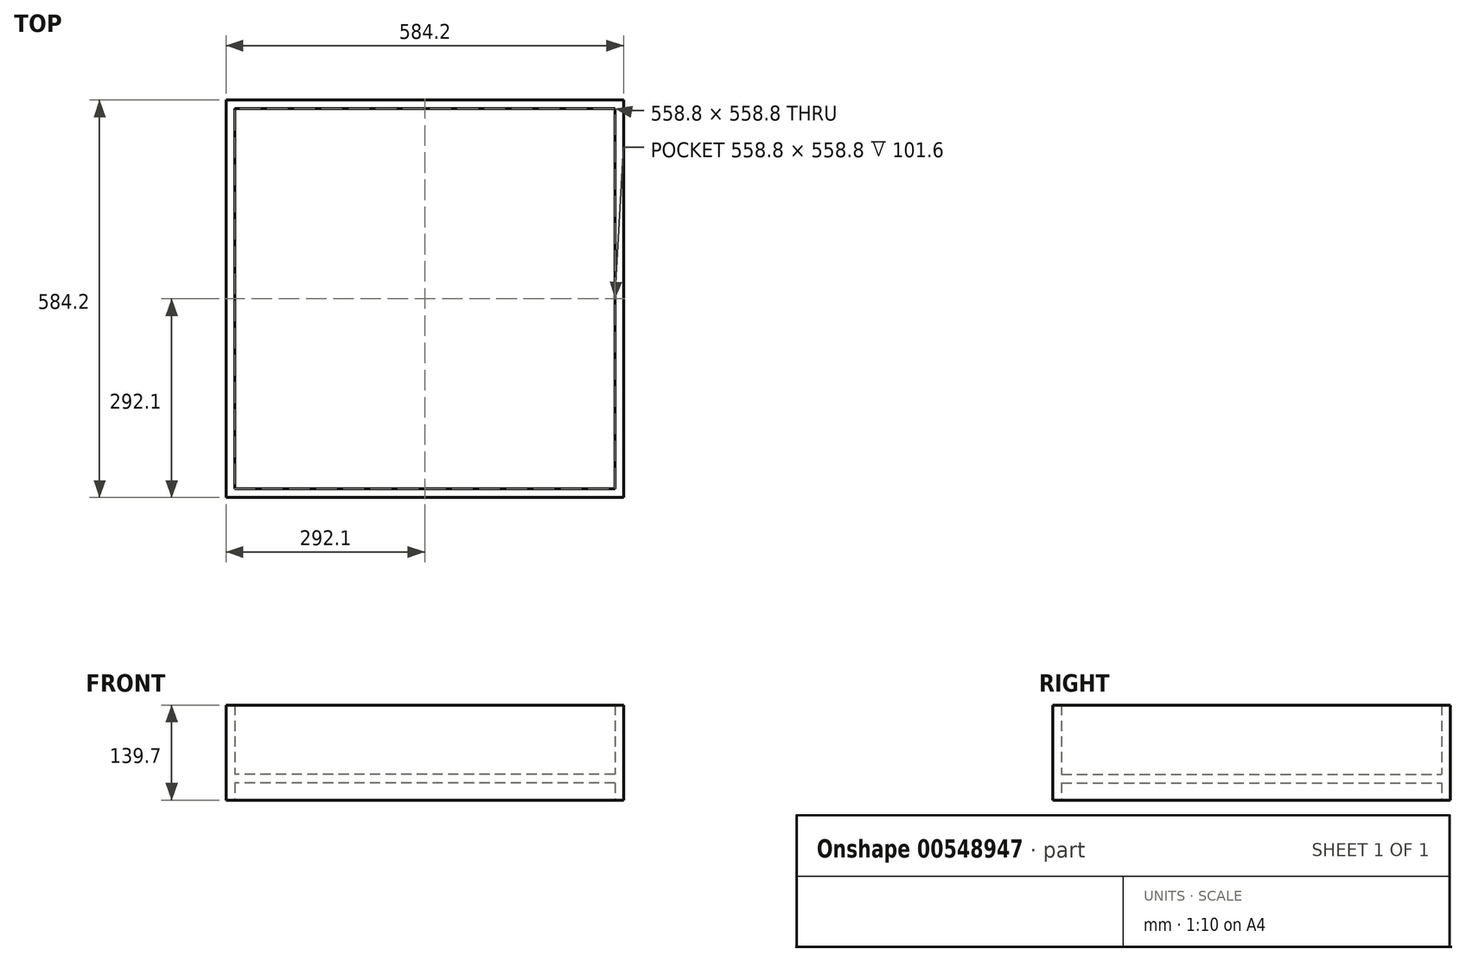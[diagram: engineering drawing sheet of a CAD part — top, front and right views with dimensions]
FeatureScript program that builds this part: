
annotation { "Feature Type Name" : "Feature", "Feature Type Description" : "" }
export const myFeature = defineFeature(function(context is Context, id is Id, definition is map)
    precondition{}
    {
        {
            var Q0;
            Q0=qCreatedBy(makeId("Top.planeOp"),FACE);
            var sketch = newSketch(context, id + "F0", { "sketchPlane" : qUnion([Q0])});
            skLineSegment(sketch, "E0.bottom", {"start": v(-292.1, 292.1) * mm, "end": v(292.1, 292.1) * mm});
            skLineSegment(sketch, "E0.top", {"start": v(-292.1, -292.1) * mm, "end": v(292.1, -292.1) * mm});
            skLineSegment(sketch, "E0.left", {"start": v(-292.1, 292.1) * mm, "end": v(-292.1, -292.1) * mm});
            skLineSegment(sketch, "E0.right", {"start": v(292.1, 292.1) * mm, "end": v(292.1, -292.1) * mm});
            skPoint(sketch, "E0.middle", {"position": v(0, 0) * mm});
            skSolve(sketch);
        }
        {
            var Q0;
            Q0 = qSketchRegion(id + "F0", true);
            extrude(context, id + "F1", {"entities" : qUnion([Q0]), "depth" : 12.7 * mm, "offsetDistance" : 25.4 * mm});
        }
        {
            var Q0;
            Q0=makeQuery(id+"F1.opExtrude","CAP_FACE",FACE,{"disambiguationData":[OSD([sQuery(id+"F0.wireOp",EDGE,"E0.bottom"),sQuery(id+"F0.wireOp",EDGE,"E0.top"),sQuery(id+"F0.wireOp",EDGE,"E0.left"),sQuery(id+"F0.wireOp",EDGE,"E0.right")])],"isStart":false});
            var sketch = newSketch(context, id + "F2", { "sketchPlane" : qUnion([Q0])});
            skLineSegment(sketch, "E1.bottom", {"start": v(-292.1, 292.1) * mm, "end": v(292.1, 292.1) * mm});
            skLineSegment(sketch, "E1.top", {"start": v(-292.1, -292.1) * mm, "end": v(292.1, -292.1) * mm});
            skLineSegment(sketch, "E1.left", {"start": v(-292.1, 292.1) * mm, "end": v(-292.1, -292.1) * mm});
            skLineSegment(sketch, "E1.right", {"start": v(292.1, 292.1) * mm, "end": v(292.1, -292.1) * mm});
            skLineSegment(sketch, "E2.bottom", {"start": v(-279.4, 279.4) * mm, "end": v(279.4, 279.4) * mm});
            skLineSegment(sketch, "E2.top", {"start": v(-279.4, -279.4) * mm, "end": v(279.4, -279.4) * mm});
            skLineSegment(sketch, "E2.left", {"start": v(-279.4, 279.4) * mm, "end": v(-279.4, -279.4) * mm});
            skLineSegment(sketch, "E2.right", {"start": v(279.4, 279.4) * mm, "end": v(279.4, -279.4) * mm});
            skSolve(sketch);
        }
        {
            var Q0;
            Q0 = qSketchRegion(id + "F2", true);
            extrude(context, id + "F3", {"entities" : qUnion([Q0]), "operationType" : NewBodyOperationType.ADD, "depth" : 101.6 * mm, "offsetDistance" : 25.4 * mm, "hasSecondDirection" : true, "secondDirectionOppositeDirection" : true, "secondDirectionDepth" : 38.1 * mm});
        }
    });
